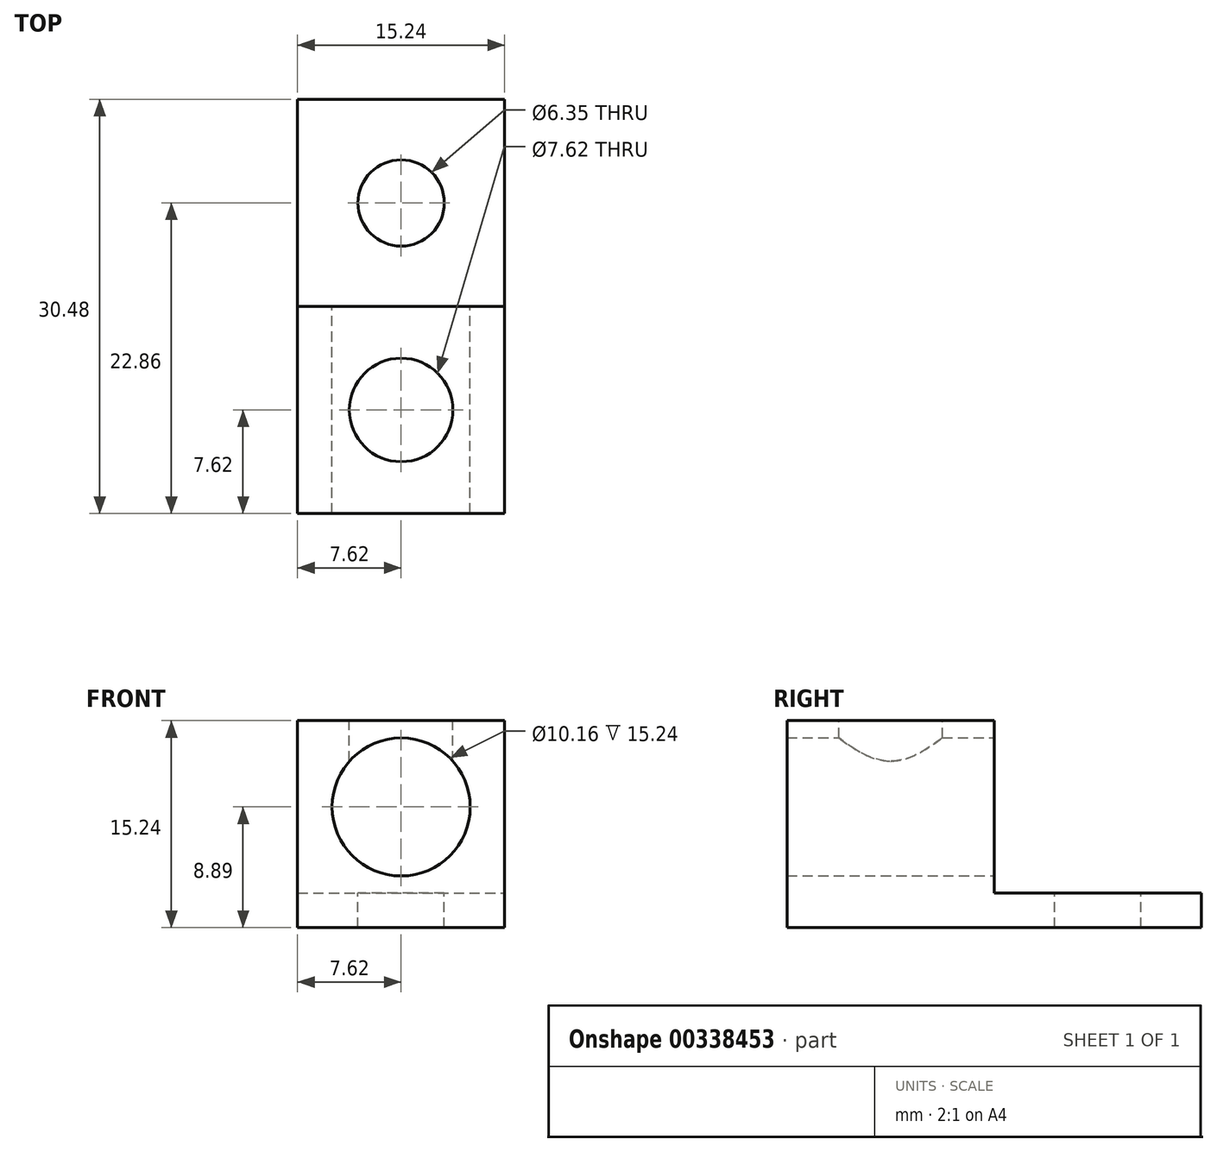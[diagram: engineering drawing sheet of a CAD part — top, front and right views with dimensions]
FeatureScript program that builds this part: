
annotation { "Feature Type Name" : "Feature", "Feature Type Description" : "" }
export const myFeature = defineFeature(function(context is Context, id is Id, definition is map)
    precondition{}
    {
        {
            var Q0;
            Q0=qCreatedBy(makeId("Top.planeOp"),FACE);
            var sketch = newSketch(context, id + "F0", { "sketchPlane" : qUnion([Q0])});
            skLineSegment(sketch, "E0.bottom", {"start": v(0, 0) * mm, "end": v(15.24, 0) * mm});
            skLineSegment(sketch, "E0.top", {"start": v(0, -30.48) * mm, "end": v(15.24, -30.48) * mm});
            skLineSegment(sketch, "E0.left", {"start": v(0, 0) * mm, "end": v(0, -30.48) * mm});
            skLineSegment(sketch, "E0.right", {"start": v(15.24, 0) * mm, "end": v(15.24, -30.48) * mm});
            skSolve(sketch);
        }
        {
            var Q0;
            Q0=makeQuery(id+"F0.imprint","IMPRINT",FACE,{"disambiguationData":[TD([[makeQuery(id+"F0.imprint","IMPRINT",EDGE,{"derivedFrom":sQuery(id+"F0.wireOp",EDGE,"E0.bottom")}),-1.0]])]});
            extrude(context, id + "F1", {"entities" : qUnion([Q0]), "depth" : 2.54 * mm});
        }
        {
            var Q0;
            Q0=makeQuery(id+"F1.opExtrude","CAP_FACE",FACE,{"disambiguationData":[OSD([sQuery(id+"F0.wireOp",EDGE,"E0.bottom"),sQuery(id+"F0.wireOp",EDGE,"E0.top"),sQuery(id+"F0.wireOp",EDGE,"E0.left"),sQuery(id+"F0.wireOp",EDGE,"E0.right")])],"isStart":false});
            var sketch = newSketch(context, id + "F2", { "sketchPlane" : qUnion([Q0])});
            skLineSegment(sketch, "E1.bottom", {"start": v(0, -30.48) * mm, "end": v(15.24, -30.48) * mm});
            skLineSegment(sketch, "E1.top", {"start": v(0, -15.24) * mm, "end": v(15.24, -15.24) * mm});
            skLineSegment(sketch, "E1.left", {"start": v(0, -30.48) * mm, "end": v(0, -15.24) * mm});
            skLineSegment(sketch, "E1.right", {"start": v(15.24, -30.48) * mm, "end": v(15.24, -15.24) * mm});
            skSolve(sketch);
        }
        {
            var Q0;
            Q0=makeQuery(id+"F2.imprint","IMPRINT",FACE,{"disambiguationData":[TD([[makeQuery(id+"F2.imprint","IMPRINT",EDGE,{"derivedFrom":sQuery(id+"F2.wireOp",EDGE,"E1.bottom")}),1.0]])]});
            extrude(context, id + "F3", {"entities" : qUnion([Q0]), "operationType" : NewBodyOperationType.ADD, "depth" : 12.7 * mm});
        }
        {
            var Q0;
            Q0=makeQuery(id+"F1.opExtrude","CAP_FACE",FACE,{"disambiguationData":[OSD([sQuery(id+"F0.wireOp",EDGE,"E0.bottom"),sQuery(id+"F0.wireOp",EDGE,"E0.top"),sQuery(id+"F0.wireOp",EDGE,"E0.left"),sQuery(id+"F0.wireOp",EDGE,"E0.right")])],"isStart":false});
            var sketch = newSketch(context, id + "F4", { "sketchPlane" : qUnion([Q0])});
            skCircle(sketch, "E2", {"center": v(7.62, -7.62) * mm, "radius": 3.18 * mm});
            skPoint(sketch, "E2.centerSnap0", {"position": v(0, -7.62) * mm});
            skPoint(sketch, "E2.centerSnap1", {"position": v(7.62, 0) * mm});
            skSolve(sketch);
        }
        {
            var Q0;
            Q0=makeQuery(id+"F4.imprint","IMPRINT",FACE,{"disambiguationData":[TD([[makeQuery(id+"F4.imprint","IMPRINT",EDGE,{"derivedFrom":sQuery(id+"F4.wireOp",EDGE,"E2")}),1.0]])]});
            extrude(context, id + "F5", {"entities" : qUnion([Q0]), "operationType" : NewBodyOperationType.REMOVE, "oppositeDirection" : true, "depth" : 25.4 * mm});
        }
        {
            var Q0;
            Q0=makeQuery(id+"F3.opExtrude","SWEPT_FACE",FACE,{"disambiguationData":[OSD([sQuery(id+"F2.wireOp",EDGE,"E1.top")])]});
            var sketch = newSketch(context, id + "F6", { "sketchPlane" : qUnion([Q0])});
            skCircle(sketch, "E3", {"center": v(-7.62, 8.9) * mm, "radius": 5.08 * mm});
            skPoint(sketch, "E3.centerSnap0", {"position": v(0, 8.9) * mm});
            skPoint(sketch, "E3.centerSnap1", {"position": v(-7.62, 15.24) * mm});
            skSolve(sketch);
        }
        {
            var Q0;
            Q0=makeQuery(id+"F6.imprint","IMPRINT",FACE,{"disambiguationData":[TD([[makeQuery(id+"F6.imprint","IMPRINT",EDGE,{"derivedFrom":sQuery(id+"F6.wireOp",EDGE,"E3")}),1.0]])]});
            extrude(context, id + "F7", {"entities" : qUnion([Q0]), "operationType" : NewBodyOperationType.REMOVE, "oppositeDirection" : true, "depth" : 25.4 * mm});
        }
        {
            var Q0;
            Q0=makeQuery(id+"F3.opExtrude","CAP_FACE",FACE,{"disambiguationData":[OSD([sQuery(id+"F2.wireOp",EDGE,"E1.bottom"),sQuery(id+"F2.wireOp",EDGE,"E1.top"),sQuery(id+"F2.wireOp",EDGE,"E1.left"),sQuery(id+"F2.wireOp",EDGE,"E1.right")])],"isStart":false});
            var sketch = newSketch(context, id + "F8", { "sketchPlane" : qUnion([Q0])});
            skCircle(sketch, "E4", {"center": v(7.62, -22.86) * mm, "radius": 3.81 * mm});
            skPoint(sketch, "E4.centerSnap0", {"position": v(7.62, -30.48) * mm});
            skPoint(sketch, "E4.centerSnap1", {"position": v(15.24, -22.86) * mm});
            skSolve(sketch);
        }
        {
            var Q0;
            Q0=makeQuery(id+"F8.imprint","IMPRINT",FACE,{"disambiguationData":[TD([[makeQuery(id+"F8.imprint","IMPRINT",EDGE,{"derivedFrom":sQuery(id+"F8.wireOp",EDGE,"E4")}),1.0]])]});
            extrude(context, id + "F9", {"entities" : qUnion([Q0]), "operationType" : NewBodyOperationType.REMOVE, "oppositeDirection" : true, "depth" : 3.56 * mm});
        }
    });
